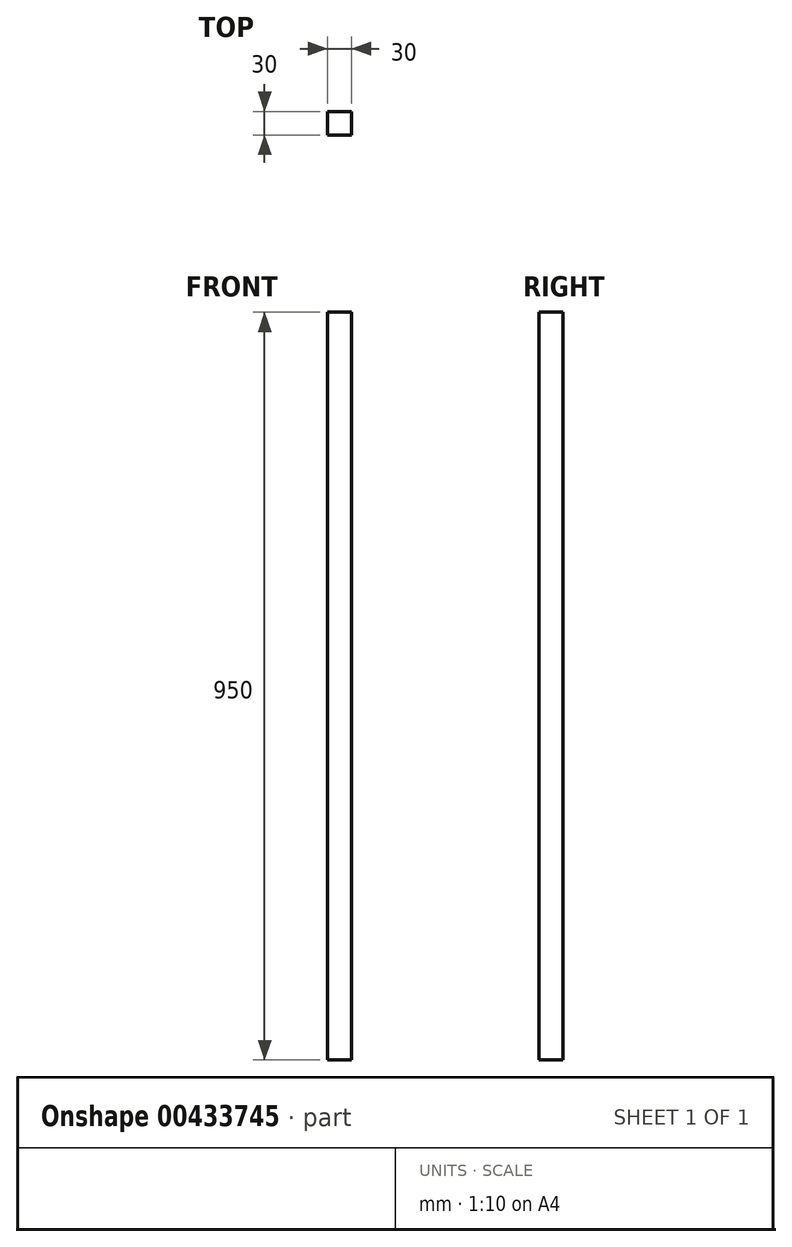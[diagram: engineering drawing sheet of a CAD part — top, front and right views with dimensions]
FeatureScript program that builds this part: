
annotation { "Feature Type Name" : "Feature", "Feature Type Description" : "" }
export const myFeature = defineFeature(function(context is Context, id is Id, definition is map)
    precondition{}
    {
        {
            var Q0;
            Q0=qCreatedBy(makeId("Front.planeOp"),FACE);
            var sketch = newSketch(context, id + "F0", { "sketchPlane" : qUnion([Q0])});
            skLineSegment(sketch, "E0.bottom", {"start": v(-75.25, -56.45) * mm, "end": v(-45.25, -56.45) * mm});
            skLineSegment(sketch, "E0.top", {"start": v(-75.25, 893.55) * mm, "end": v(-45.25, 893.55) * mm});
            skLineSegment(sketch, "E0.left", {"start": v(-75.25, -56.45) * mm, "end": v(-75.25, 893.55) * mm});
            skLineSegment(sketch, "E0.right", {"start": v(-45.25, -56.45) * mm, "end": v(-45.25, 893.55) * mm});
            skSolve(sketch);
        }
        {
            var Q0;
            Q0 = qSketchRegion(id + "F0", true);
            extrude(context, id + "F1", {"entities" : qUnion([Q0]), "depth" : 30 * mm, "offsetDistance" : 25 * mm});
        }
    });
